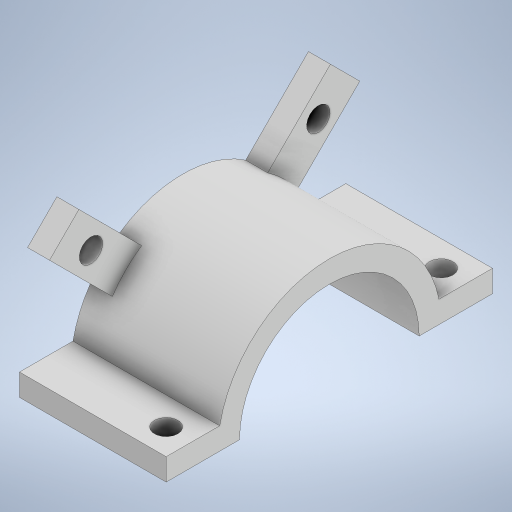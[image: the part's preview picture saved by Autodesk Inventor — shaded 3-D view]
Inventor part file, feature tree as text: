
AUTODESK INVENTOR PART (.ipt)
format: ipt  version: 2023 (Build 270158000, 158)  size: 302,592 bytes
history: native  units: mm
features: sketch x5, extrude x3, mirror x2, hole x2
ambient origin geometry x8: Origin, YZ Plane, XZ Plane, XY Plane, X Axis, Y Axis, Z Axis, Center Point
bodies: Volumenkörper1 (feature_tree)
feature tree (12):
  extrude  "Extrusion1"  Depth=15.25mm
  extrude  "Extrusion4"  Depth=20.0mm
  mirror  "Spiegeln4"
  hole  "Bohrung3"  [1 undecoded]
  extrude  "Extrusion5"  Depth=3.0mm TaperAngle=0.0deg
  hole  "Bohrung4"  [1 undecoded]
  mirror  "Spiegeln5"
  sketch  "Skizze1"  dims[d0=12.25mm d1=15.25mm]
  sketch  "Skizze7"  dims[d2=20.0mm d3=0.0mm d40=12.097mm]
  sketch  "Skizze8"  dims[d41=135.0deg d42=8.596mm]
  sketch  "Skizze9"  dims[d43=5.657mm d44=3.0mm d45=0.0mm]
  sketch  "Skizze10"  dims[d46=3.2mm d47=6.0mm d48=4.0mm d49=2.0mm d50=90.0deg d51=8.0mm d52=20.594885mm d53=5.162mm d54=5.162mm d55=2.8285mm d56=2.8285mm d57=7.0mm d58=3.0mm d59=20.0mm d60=0.0mm d61=3.2mm d62=6.0mm d63=4.0mm d64=2.0mm d65=90.0deg d66=8.0mm d67=20.594885mm d68=3.5mm d69=3.5mm]
note: 2 required parameter values undecoded (feature->parameter linkage not recoverable at this tier; creation-order binding heuristic only, values carry confidence <= 0.55)
